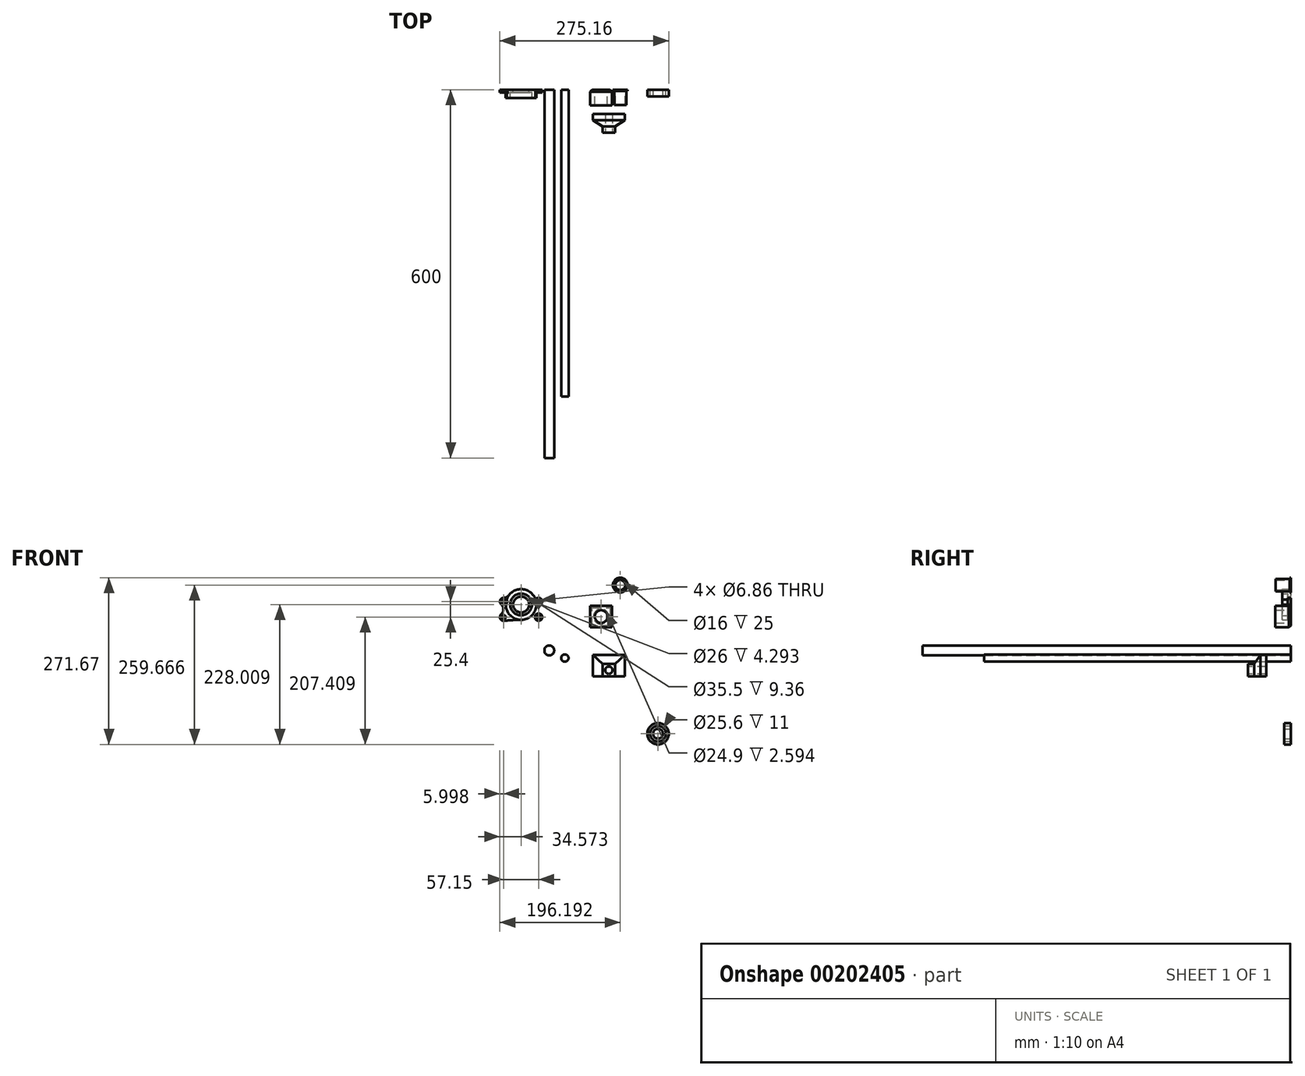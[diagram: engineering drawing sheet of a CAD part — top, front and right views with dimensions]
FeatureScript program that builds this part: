
annotation { "Feature Type Name" : "Feature", "Feature Type Description" : "" }
export const myFeature = defineFeature(function(context is Context, id is Id, definition is map)
    precondition{}
    {
        {
            var Q0;
            Q0=qCreatedBy(makeId("Front.planeOp"),FACE);
            var sketch = newSketch(context, id + "F0", { "sketchPlane" : qUnion([Q0])});
            skCircle(sketch, "E0", {"center": v(-55.77, 42.1) * mm, "radius": 8 * mm});
            skSolve(sketch);
        }
        {
            var Q0;
            Q0=qCreatedBy(makeId("Front.planeOp"),FACE);
            var sketch = newSketch(context, id + "F1", { "sketchPlane" : qUnion([Q0])});
            skCircle(sketch, "E1", {"center": v(-30.32, 29.76) * mm, "radius": 6 * mm});
            skSolve(sketch);
        }
        {
            var Q0;
            Q0=makeQuery(id+"F0.imprint","IMPRINT",FACE,{"disambiguationData":[TD([[makeQuery(id+"F0.imprint","IMPRINT",EDGE,{"derivedFrom":sQuery(id+"F0.wireOp",EDGE,"E0")}),1.0]])]});
            extrude(context, id + "F2", {"entities" : qUnion([Q0]), "depth" : 600 * mm});
        }
        {
            var Q0;
            Q0=makeQuery(id+"F1.imprint","IMPRINT",FACE,{"disambiguationData":[TD([[makeQuery(id+"F1.imprint","IMPRINT",EDGE,{"derivedFrom":sQuery(id+"F1.wireOp",EDGE,"E1")}),1.0]])]});
            extrude(context, id + "F3", {"entities" : qUnion([Q0]), "depth" : 500 * mm});
        }
        {
            var Q0;
            Q0=qCreatedBy(makeId("Top.planeOp"),FACE);
            var sketch = newSketch(context, id + "F4", { "sketchPlane" : qUnion([Q0])});
            skLineSegment(sketch, "E2", {"start": v(15.55, -39.74) * mm, "end": v(67.05, -39.74) * mm});
            skLineSegment(sketch, "E3", {"start": v(67.05, -39.74) * mm, "end": v(67.05, -49.74) * mm});
            skLineSegment(sketch, "E4", {"start": v(67.05, -49.74) * mm, "end": v(51.3, -59.74) * mm});
            skLineSegment(sketch, "E5", {"start": v(51.3, -59.74) * mm, "end": v(31.3, -59.74) * mm});
            skLineSegment(sketch, "E6", {"start": v(31.3, -59.74) * mm, "end": v(15.55, -49.74) * mm});
            skLineSegment(sketch, "E7", {"start": v(15.55, -49.74) * mm, "end": v(15.55, -39.74) * mm});
            skLineSegment(sketch, "E8", {"start": v(51.3, -59.74) * mm, "end": v(51.3, -69.74) * mm});
            skLineSegment(sketch, "E9", {"start": v(51.3, -69.74) * mm, "end": v(31.3, -69.74) * mm});
            skLineSegment(sketch, "E10", {"start": v(31.3, -69.74) * mm, "end": v(31.3, -59.74) * mm});
            skSolve(sketch);
        }
        {
            var Q0;
            Q0=makeQuery(id+"F4.imprint","IMPRINT",FACE,{"disambiguationData":[TD([[makeQuery(id+"F4.imprint","IMPRINT",EDGE,{"derivedFrom":sQuery(id+"F4.wireOp",EDGE,"E5")}),1.0]])]});
            extrude(context, id + "F5", {"entities" : qUnion([Q0]), "depth" : 20 * mm});
        }
        {
            var Q0;
            Q0=makeQuery(id+"F4.imprint","IMPRINT",FACE,{"disambiguationData":[TD([[makeQuery(id+"F4.imprint","IMPRINT",EDGE,{"derivedFrom":sQuery(id+"F4.wireOp",EDGE,"E2")}),-1.0]])]});
            extrude(context, id + "F6", {"entities" : qUnion([Q0]), "operationType" : NewBodyOperationType.ADD, "depth" : 35 * mm});
        }
        {
            var Q0;
            Q0=qCreatedBy(makeId("Right.planeOp"),FACE);
            var sketch = newSketch(context, id + "F7", { "sketchPlane" : qUnion([Q0])});
            skLineSegment(sketch, "E11", {"start": v(-59.74, 0) * mm, "end": v(-59.74, 20) * mm});
            skLineSegment(sketch, "E12", {"start": v(-59.74, 20) * mm, "end": v(-49.74, 35) * mm});
            skLineSegment(sketch, "E13", {"start": v(-49.74, 35) * mm, "end": v(-59.74, 35) * mm});
            skLineSegment(sketch, "E14", {"start": v(-59.74, 35) * mm, "end": v(-59.74, 20) * mm});
            skSolve(sketch);
        }
        {
            var Q0;
            Q0=makeQuery(id+"F7.imprint","IMPRINT",FACE,{"disambiguationData":[TD([[makeQuery(id+"F7.imprint","IMPRINT",EDGE,{"derivedFrom":sQuery(id+"F7.wireOp",EDGE,"E12")}),1.0]])]});
            extrude(context, id + "F8", {"entities" : qUnion([Q0]), "operationType" : NewBodyOperationType.REMOVE, "endBound" : BoundingType.THROUGH_ALL, "depth" : 25.4 * mm});
        }
        {
            var Q0;
            Q0=makeQuery(id+"F5.opExtrude","SWEPT_FACE",FACE,{"disambiguationData":[OSD([sQuery(id+"F4.wireOp",EDGE,"E9")])]});
            var sketch = newSketch(context, id + "F9", { "sketchPlane" : qUnion([Q0])});
            skCircle(sketch, "E15", {"center": v(41.3, 10) * mm, "radius": 6 * mm});
            skLineSegment(sketch, "E16", {"start": v(41.3, 10) * mm, "end": v(31.3, 10) * mm, "construction": true});
            skSolve(sketch);
        }
        {
            var Q0;
            Q0=makeQuery(id+"F9.imprint","IMPRINT",FACE,{"disambiguationData":[TD([[makeQuery(id+"F9.imprint","IMPRINT",EDGE,{"derivedFrom":sQuery(id+"F9.wireOp",EDGE,"E15")}),1.0]])]});
            extrude(context, id + "F10", {"entities" : qUnion([Q0]), "operationType" : NewBodyOperationType.REMOVE, "endBound" : BoundingType.THROUGH_ALL, "oppositeDirection" : true, "depth" : 25.4 * mm});
        }
        {
            var Q0;
            Q0=qCreatedBy(makeId("Front.planeOp"),FACE);
            var sketch = newSketch(context, id + "F11", { "sketchPlane" : qUnion([Q0])});
            skLineSegment(sketch, "E17", {"start": v(11.05, 114.9) * mm, "end": v(46.32, 114.9) * mm});
            skLineSegment(sketch, "E18", {"start": v(46.32, 114.9) * mm, "end": v(46.32, 79.62) * mm});
            skLineSegment(sketch, "E19", {"start": v(46.32, 79.62) * mm, "end": v(11.05, 79.62) * mm});
            skLineSegment(sketch, "E20", {"start": v(11.05, 79.62) * mm, "end": v(11.05, 114.9) * mm});
            skSolve(sketch);
        }
        {
            var Q0;
            Q0=makeQuery(id+"F11.imprint","IMPRINT",FACE,{"disambiguationData":[TD([[makeQuery(id+"F11.imprint","IMPRINT",EDGE,{"derivedFrom":sQuery(id+"F11.wireOp",EDGE,"E17")}),-1.0]])]});
            extrude(context, id + "F12", {"entities" : qUnion([Q0]), "depth" : 22.88 * mm});
        }
        {
            var Q0;
            Q0=makeQuery(id+"F12.opExtrude","CAP_FACE",FACE,{"disambiguationData":[OSD([sQuery(id+"F11.wireOp",EDGE,"E17"),sQuery(id+"F11.wireOp",EDGE,"E18"),sQuery(id+"F11.wireOp",EDGE,"E19"),sQuery(id+"F11.wireOp",EDGE,"E20")])],"isStart":true});
            var sketch = newSketch(context, id + "F13", { "sketchPlane" : qUnion([Q0])});
            skCircle(sketch, "E21", {"center": v(-28.68, 97.25) * mm, "radius": 10.38 * mm});
            skLineSegment(sketch, "E22", {"start": v(-46.32, 97.25) * mm, "end": v(-11.05, 97.25) * mm, "construction": true});
            skSolve(sketch);
        }
        {
            var Q0;
            Q0=makeQuery(id+"F13.imprint","IMPRINT",FACE,{"disambiguationData":[TD([[makeQuery(id+"F13.imprint","IMPRINT",EDGE,{"derivedFrom":sQuery(id+"F13.wireOp",EDGE,"E21")}),1.0]])]});
            extrude(context, id + "F14", {"entities" : qUnion([Q0]), "operationType" : NewBodyOperationType.REMOVE, "endBound" : BoundingType.THROUGH_ALL, "oppositeDirection" : true, "depth" : 25.4 * mm});
        }
        {
            var Q0;
            Q0=qCreatedBy(makeId("Front.planeOp"),FACE);
            var sketch = newSketch(context, id + "F15", { "sketchPlane" : qUnion([Q0])});
            skCircle(sketch, "E23", {"center": v(28.68, 97.25) * mm, "radius": 12.45 * mm});
            skLineSegment(sketch, "E24", {"start": v(46.32, 97.25) * mm, "end": v(11.05, 97.25) * mm, "construction": true});
            skSolve(sketch);
        }
        {
            var Q0;
            Q0=qSketchRegion(id+"F15",true);
            extrude(context, id + "F16", {"entities" : qUnion([Q0]), "operationType" : NewBodyOperationType.REMOVE, "depth" : 2.6 * mm});
        }
        {
            var Q0;
            Q0=makeQuery(id+"F12.opExtrude","CAP_EDGE",EDGE,{"disambiguationData":[OSD([sQuery(id+"F11.wireOp",EDGE,"E18")])],"isStart":true});
            var Q1;
            Q1=makeQuery(id+"F12.opExtrude","CAP_EDGE",EDGE,{"disambiguationData":[OSD([sQuery(id+"F11.wireOp",EDGE,"E17")])],"isStart":true});
            var Q2;
            Q2=makeQuery(id+"F12.opExtrude","CAP_EDGE",EDGE,{"disambiguationData":[OSD([sQuery(id+"F11.wireOp",EDGE,"E20")])],"isStart":true});
            var Q3;
            Q3=makeQuery(id+"F12.opExtrude","CAP_EDGE",EDGE,{"disambiguationData":[OSD([sQuery(id+"F11.wireOp",EDGE,"E19")])],"isStart":true});
            chamfer(context, id + "F17", {"entities" : qUnion([Q0, Q1, Q2, Q3]), "width" : 3.12 * mm, "tangentPropagation" : true});
        }
        {
            var Q0;
            Q0=qCreatedBy(makeId("Front.planeOp"),FACE);
            var sketch = newSketch(context, id + "F18", { "sketchPlane" : qUnion([Q0])});
            skCircle(sketch, "E25", {"center": v(59.92, 148.64) * mm, "radius": 8 * mm});
            skCircle(sketch, "E26", {"center": v(59.92, 148.64) * mm, "radius": 10 * mm});
            skCircle(sketch, "E27", {"center": v(59.92, 148.64) * mm, "radius": 12 * mm});
            skSolve(sketch);
        }
        {
            var Q0;
            Q0=makeQuery(id+"F18.imprint","IMPRINT",FACE,{"disambiguationData":[TD([[makeQuery(id+"F18.imprint","IMPRINT",EDGE,{"derivedFrom":sQuery(id+"F18.wireOp",EDGE,"E25")}),-1.0]])]});
            extrude(context, id + "F19", {"entities" : qUnion([Q0]), "depth" : 25 * mm});
        }
        {
            var Q0;
            Q0=makeQuery(id+"F18.imprint","IMPRINT",FACE,{"disambiguationData":[TD([[makeQuery(id+"F18.imprint","IMPRINT",EDGE,{"derivedFrom":sQuery(id+"F18.wireOp",EDGE,"E26")}),-1.0]])]});
            extrude(context, id + "F20", {"entities" : qUnion([Q0]), "operationType" : NewBodyOperationType.ADD, "depth" : 2 * mm});
        }
        {
            var Q0;
            Q0=makeQuery(id+"F12.opExtrude","CAP_FACE",FACE,{"disambiguationData":[OSD([sQuery(id+"F11.wireOp",EDGE,"E17"),sQuery(id+"F11.wireOp",EDGE,"E18"),sQuery(id+"F11.wireOp",EDGE,"E19"),sQuery(id+"F11.wireOp",EDGE,"E20")])],"isStart":false});
            extrude(context, id + "F21", {"entities" : qUnion([Q0]), "operationType" : NewBodyOperationType.ADD, "depth" : 2.75 * mm});
        }
        {
            var Q0;
            Q0=qCreatedBy(makeId("Front.planeOp"),FACE);
            var sketch = newSketch(context, id + "F22", { "sketchPlane" : qUnion([Q0])});
            skCircle(sketch, "E28", {"center": v(121.4, -93.53) * mm, "radius": 8 * mm});
            skCircle(sketch, "E29", {"center": v(121.4, -93.53) * mm, "radius": 17.5 * mm});
            skCircle(sketch, "E30", {"center": v(121.4, -93.53) * mm, "radius": 12.8 * mm});
            skSolve(sketch);
        }
        {
            var Q0;
            Q0=makeQuery(id+"F22.imprint","IMPRINT",FACE,{"disambiguationData":[TD([[makeQuery(id+"F22.imprint","IMPRINT",EDGE,{"derivedFrom":sQuery(id+"F22.wireOp",EDGE,"E29")}),1.0]])]});
            extrude(context, id + "F23", {"entities" : qUnion([Q0]), "depth" : 11 * mm});
        }
        {
            var Q0;
            Q0=makeQuery(id+"F22.imprint","IMPRINT",FACE,{"disambiguationData":[TD([[makeQuery(id+"F22.imprint","IMPRINT",EDGE,{"derivedFrom":sQuery(id+"F22.wireOp",EDGE,"E28")}),-1.0]])]});
            extrude(context, id + "F24", {"entities" : qUnion([Q0]), "depth" : 11 * mm});
        }
        {
            var Q0;
            Q0=qCreatedBy(makeId("Front.planeOp"),FACE);
            var sketch = newSketch(context, id + "F25", { "sketchPlane" : qUnion([Q0])});
            skCircle(sketch, "E31", {"center": v(-130.27, 121.78) * mm, "radius": 3.43 * mm});
            skCircle(sketch, "E32", {"center": v(-130.27, 96.38) * mm, "radius": 3.43 * mm});
            skCircle(sketch, "E33", {"center": v(-73.12, 96.38) * mm, "radius": 3.43 * mm});
            skCircle(sketch, "E34", {"center": v(-73.12, 121.78) * mm, "radius": 3.43 * mm});
            skCircle(sketch, "E35", {"center": v(-101.7, 116.98) * mm, "radius": 13 * mm});
            skCircle(sketch, "E36", {"center": v(-101.7, 116.98) * mm, "radius": 25 * mm});
            skCircle(sketch, "E37", {"center": v(-130.27, 121.78) * mm, "radius": 6 * mm});
            skCircle(sketch, "E38", {"center": v(-130.27, 96.38) * mm, "radius": 6 * mm});
            skCircle(sketch, "E39", {"center": v(-73.12, 121.78) * mm, "radius": 6 * mm});
            skCircle(sketch, "E40", {"center": v(-73.12, 96.38) * mm, "radius": 6 * mm});
            skArc(sketch, "E41", {"start": v(-134.24, 100.88) * mm, "mid": v(-130.53, 109.08) * mm, "end": v(-134.24, 117.28) * mm});
            skArc(sketch, "E42", {"start": v(-73.8, 90.42) * mm, "mid": v(-101.7, 91.98) * mm, "end": v(-129.6, 90.42) * mm});
            skArc(sketch, "E43", {"start": v(-130.27, 127.78) * mm, "mid": v(-125.44, 128.91) * mm, "end": v(-121.62, 132.08) * mm});
            skLineSegment(sketch, "E44", {"start": v(-101.7, 116.98) * mm, "end": v(-101.7, 77.56) * mm, "construction": true});
            skArc(sketch, "E45.0.MirrorCS", {"start": v(-69.16, 100.88) * mm, "mid": v(-72.86, 109.08) * mm, "end": v(-69.16, 117.28) * mm});
            skArc(sketch, "E46.0.MirrorCS", {"start": v(-73.12, 127.78) * mm, "mid": v(-77.95, 128.91) * mm, "end": v(-81.77, 132.08) * mm});
            skCircle(sketch, "E47", {"center": v(-101.7, 116.98) * mm, "radius": 17.75 * mm});
            skSolve(sketch);
        }
        {
            var Q0;
            Q0=makeQuery(id+"F25.imprint","IMPRINT",FACE,{"disambiguationData":[TD([[makeQuery(id+"F25.imprint","IMPRINT",EDGE,{"derivedFrom":sQuery(id+"F25.wireOp",EDGE,"E35")}),-1.0]])]});
            extrude(context, id + "F26", {"entities" : qUnion([Q0]), "depth" : 4.3 * mm});
        }
        {
            var Q0;
            Q0=makeQuery(id+"F25.imprint","IMPRINT",FACE,{"disambiguationData":[TD([[makeQuery(id+"F25.imprint","IMPRINT",EDGE,{"derivedFrom":sQuery(id+"F25.wireOp",EDGE,"E47")}),-1.0]])]});
            extrude(context, id + "F27", {"entities" : qUnion([Q0]), "operationType" : NewBodyOperationType.ADD, "depth" : 13.65 * mm});
        }
        {
            var Q0;
            {var subQ0=sQuery(id+"F25.wireOp",EDGE,"E45.0.MirrorCS");Q0=makeQuery(id+"F25.imprint","IMPRINT",FACE,{"disambiguationData":[TD([[makeQuery(id+"F25.imprint","IMPRINT",EDGE,{"derivedFrom":subQ0}),1.0]])]});}
            var Q1;
            Q1=makeQuery(id+"F25.imprint","IMPRINT",FACE,{"disambiguationData":[TD([[makeQuery(id+"F25.imprint","IMPRINT",EDGE,{"derivedFrom":sQuery(id+"F25.wireOp",EDGE,"E33")}),-1.0]])]});
            var Q2;
            Q2=makeQuery(id+"F25.imprint","IMPRINT",FACE,{"disambiguationData":[TD([[makeQuery(id+"F25.imprint","IMPRINT",EDGE,{"derivedFrom":sQuery(id+"F25.wireOp",EDGE,"E34")}),-1.0]])]});
            var Q3;
            {var subQ0=sQuery(id+"F25.wireOp",EDGE,"E46.0.MirrorCS");Q3=makeQuery(id+"F25.imprint","IMPRINT",FACE,{"disambiguationData":[TD([[makeQuery(id+"F25.imprint","IMPRINT",EDGE,{"derivedFrom":subQ0}),1.0]])]});}
            var Q4;
            {var subQ5=sQuery(id+"F25.wireOp",EDGE,"E41");Q4=makeQuery(id+"F25.imprint","IMPRINT",FACE,{"disambiguationData":[TD([[makeQuery(id+"F25.imprint","IMPRINT",EDGE,{"derivedFrom":subQ5}),-1.0]])]});}
            var Q5;
            {var subQ0=sQuery(id+"F25.wireOp",EDGE,"E43");Q5=makeQuery(id+"F25.imprint","IMPRINT",FACE,{"disambiguationData":[TD([[makeQuery(id+"F25.imprint","IMPRINT",EDGE,{"derivedFrom":subQ0}),-1.0]])]});}
            var Q6;
            Q6=makeQuery(id+"F25.imprint","IMPRINT",FACE,{"disambiguationData":[TD([[makeQuery(id+"F25.imprint","IMPRINT",EDGE,{"derivedFrom":sQuery(id+"F25.wireOp",EDGE,"E31")}),-1.0]])]});
            var Q7;
            Q7=makeQuery(id+"F25.imprint","IMPRINT",FACE,{"disambiguationData":[TD([[makeQuery(id+"F25.imprint","IMPRINT",EDGE,{"derivedFrom":sQuery(id+"F25.wireOp",EDGE,"E32")}),-1.0]])]});
            var Q8;
            {var subQ0=sQuery(id+"F25.wireOp",EDGE,"E39");var subQ1=sQuery(id+"F25.wireOp",EDGE,"E36");var subQ3=makeQuery(id+"F25.imprint","INTERSECT",VERTEX,{"disambiguationData":[OD(0.0)],"derivedFrom":[subQ1,subQ0]});Q8=makeQuery(id+"F25.imprint","IMPRINT",FACE,{"disambiguationData":[TD([[makeQuery(id+"F25.imprint","IMPRINT",EDGE,{"disambiguationData":[TD([[subQ3,1.0]])],"derivedFrom":subQ1}),1.0]])]});}
            var Q9;
            {var subQ0=sQuery(id+"F25.wireOp",EDGE,"E37");var subQ1=sQuery(id+"F25.wireOp",EDGE,"E36");var subQ3=makeQuery(id+"F25.imprint","INTERSECT",VERTEX,{"disambiguationData":[OD(0.0)],"derivedFrom":[subQ1,subQ0]});Q9=makeQuery(id+"F25.imprint","IMPRINT",FACE,{"disambiguationData":[TD([[makeQuery(id+"F25.imprint","IMPRINT",EDGE,{"disambiguationData":[TD([[subQ3,-1.0]])],"derivedFrom":subQ1}),1.0]])]});}
            extrude(context, id + "F28", {"entities" : qUnion([Q0, Q1, Q2, Q3, Q4, Q5, Q6, Q7, Q8, Q9]), "operationType" : NewBodyOperationType.ADD, "depth" : 4.76 * mm});
        }
    });
